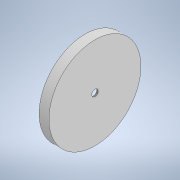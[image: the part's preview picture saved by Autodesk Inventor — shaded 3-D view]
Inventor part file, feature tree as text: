
AUTODESK INVENTOR PART (.ipt)
format: ipt  version: 2020 (Build 240168000, 168)  size: 122,880 bytes
history: native  units: mm
features: revolve x1, sketch x1
ambient origin geometry x8: Origin, YZ Plane, XZ Plane, XY Plane, X Axis, Y Axis, Z Axis, Center Point
bodies: Solid1 (feature_tree)
feature tree (2):
  revolve  "Revolution1"  Angle=90.0deg
  sketch  "Sketch1"  dims[d7=5.0mm d11=90.0deg d28=5.0mm d29=2.0mm d30=13.5mm d31=72.5mm]
